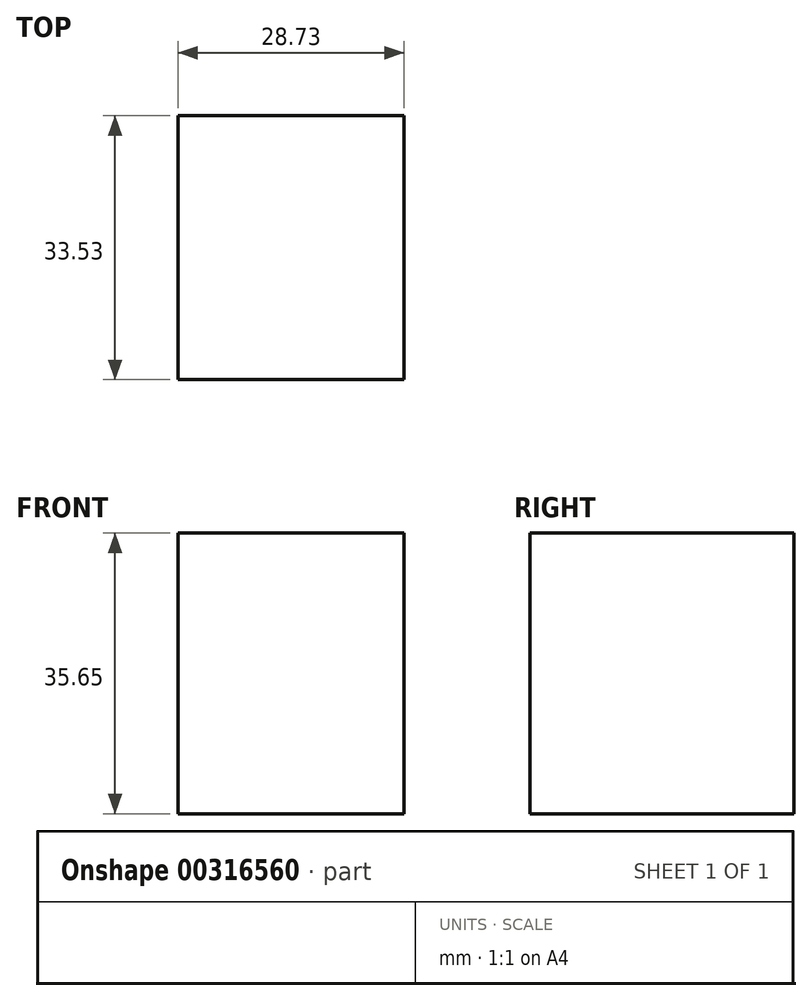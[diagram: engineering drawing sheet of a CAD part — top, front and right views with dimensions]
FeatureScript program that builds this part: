
annotation { "Feature Type Name" : "Feature", "Feature Type Description" : "" }
export const myFeature = defineFeature(function(context is Context, id is Id, definition is map)
    precondition{}
    {
        {
            var Q0;
            Q0=qCreatedBy(makeId("Front.planeOp"),FACE);
            var sketch = newSketch(context, id + "F0", { "sketchPlane" : qUnion([Q0])});
            skLineSegment(sketch, "E0.bottom", {"start": v(-103.67, 46.7) * mm, "end": v(-74.94, 46.7) * mm});
            skLineSegment(sketch, "E0.top", {"start": v(-103.67, 11.05) * mm, "end": v(-74.94, 11.05) * mm});
            skLineSegment(sketch, "E0.left", {"start": v(-103.67, 46.7) * mm, "end": v(-103.67, 11.05) * mm});
            skLineSegment(sketch, "E0.right", {"start": v(-74.94, 46.7) * mm, "end": v(-74.94, 11.05) * mm});
            skSolve(sketch);
        }
        {
            var Q0;
            Q0=makeQuery(id+"F0.imprint","IMPRINT",FACE,{"disambiguationData":[TD([[makeQuery(id+"F0.imprint","IMPRINT",EDGE,{"derivedFrom":sQuery(id+"F0.wireOp",EDGE,"E0.bottom")}),-1.0]])]});
            extrude(context, id + "F1", {"entities" : qUnion([Q0]), "depth" : 33.53 * mm});
        }
    });
